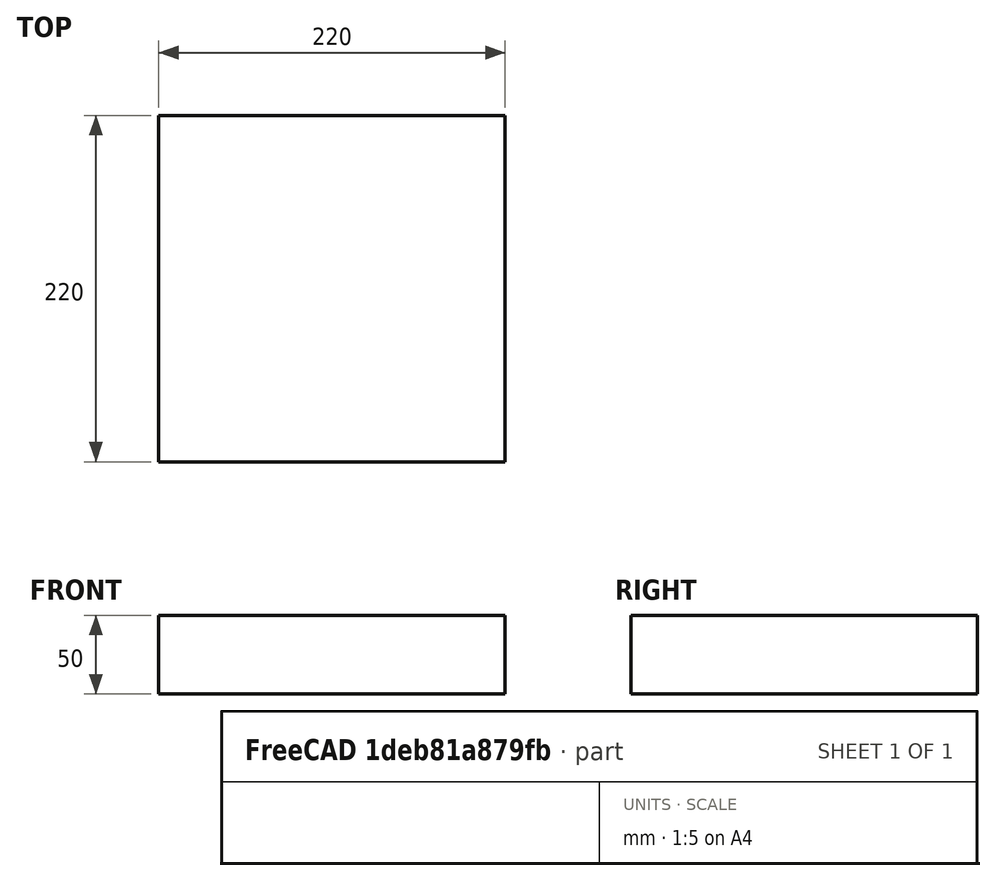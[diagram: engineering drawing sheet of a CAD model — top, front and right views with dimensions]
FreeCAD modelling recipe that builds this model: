
FCSTD DOCUMENT  (FreeCAD 0.15R4671 (Git))
Label: Square Bar 220 EN10059 S235JR
License: All rights reserved
LicenseURL: http://en.wikipedia.org/wiki/All_rights_reserved
objects: Sketcher::SketchObject×1, Part::Extrusion×1
note: 2 computed .brp shape members not serialized (recipe doc carries the construction recipe); baked Part::Feature solids carry a one-line shape summary decoded from their .brp

FEATURE [Sketcher::SketchObject] Sketch
  sketch-geometry (4):
    g0: LineSegment StartX=-110 StartY=-110 StartZ=0 EndX=110 EndY=-110 EndZ=0
    g1: LineSegment StartX=110 StartY=-110 StartZ=0 EndX=110 EndY=110 EndZ=0
    g2: LineSegment StartX=110 StartY=110 StartZ=0 EndX=-110 EndY=110 EndZ=0
    g3: LineSegment StartX=-110 StartY=110 StartZ=0 EndX=-110 EndY=-110 EndZ=0
  constraints (12):
    c: Coincident(g0,g1)
    c: Coincident(g1,g2)
    c: Coincident(g2,g3)
    c: Coincident(g3,g0)
    c: Horizontal(g0)
    c: Horizontal(g2)
    c: Vertical(g1)
    c: Vertical(g3)
    c: Symmetric(g1,g0,g-1)
    c: Symmetric(g2,g1,g-2)
    c: Equal(g1,g2)
    c: DistanceY(g1) = 220
FEATURE [Part::Extrusion] Extrude  label="Square Bar 220 EN10059 S235JR"
  Base = -> Sketch
  Dir = (0,0,50)
  Solid = true
